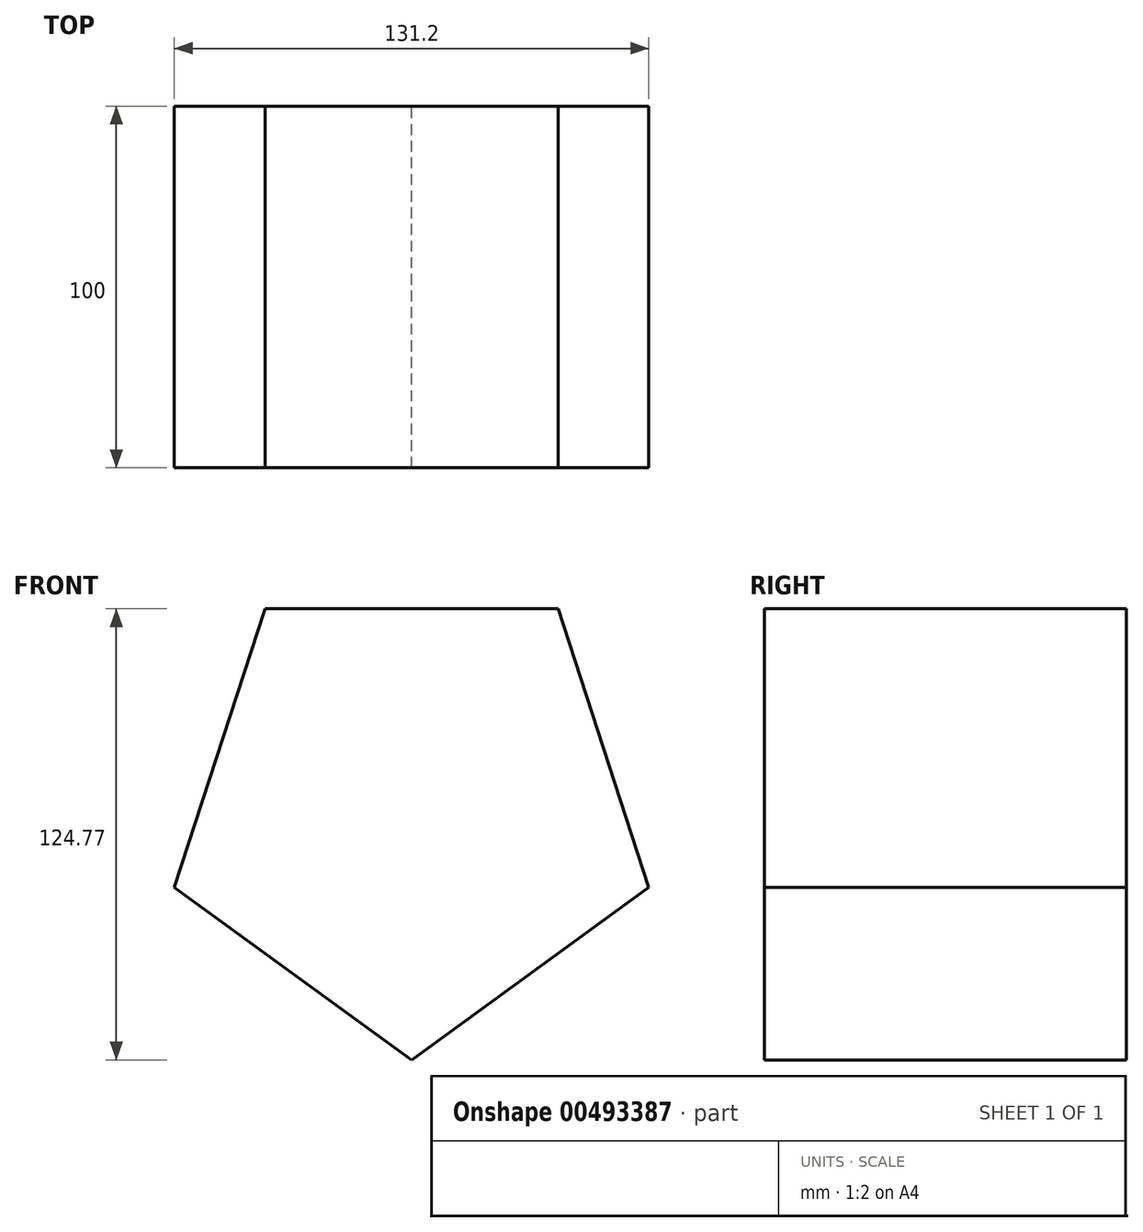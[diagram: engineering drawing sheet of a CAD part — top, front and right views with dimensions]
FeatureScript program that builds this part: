
annotation { "Feature Type Name" : "Feature", "Feature Type Description" : "" }
export const myFeature = defineFeature(function(context is Context, id is Id, definition is map)
    precondition{}
    {
        {
            var Q0;
            Q0=qCreatedBy(makeId("Front.planeOp"),FACE);
            var sketch = newSketch(context, id + "F0", { "sketchPlane" : qUnion([Q0])});
            skCircle(sketch, "E0.cCircle", {"center": v(0, 0) * mm, "radius": 55.8 * mm, "construction": true});
            skLineSegment(sketch, "E0.0", {"start": v(-40.54, 55.8) * mm, "end": v(40.54, 55.8) * mm});
            skLineSegment(sketch, "E0.1", {"start": v(40.54, 55.8) * mm, "end": v(65.6, -21.31) * mm});
            skLineSegment(sketch, "E0.2", {"start": v(65.6, -21.31) * mm, "end": v(0, -68.97) * mm});
            skLineSegment(sketch, "E0.3", {"start": v(0, -68.97) * mm, "end": v(-65.6, -21.31) * mm});
            skLineSegment(sketch, "E0.4", {"start": v(-65.6, -21.31) * mm, "end": v(-40.54, 55.8) * mm});
            skPoint(sketch, "E0.0.midPoint", {"position": v(0, 55.8) * mm});
            skSolve(sketch);
        }
        {
            var Q0;
            Q0=makeQuery(id+"F0.imprint","IMPRINT",FACE,{"disambiguationData":[TD([[makeQuery(id+"F0.imprint","IMPRINT",EDGE,{"derivedFrom":sQuery(id+"F0.wireOp",EDGE,"E0.0")}),-1.0]])]});
            extrude(context, id + "F1", {"entities" : qUnion([Q0]), "endBound" : BoundingType.SYMMETRIC, "depth" : 100 * mm});
        }
    });
